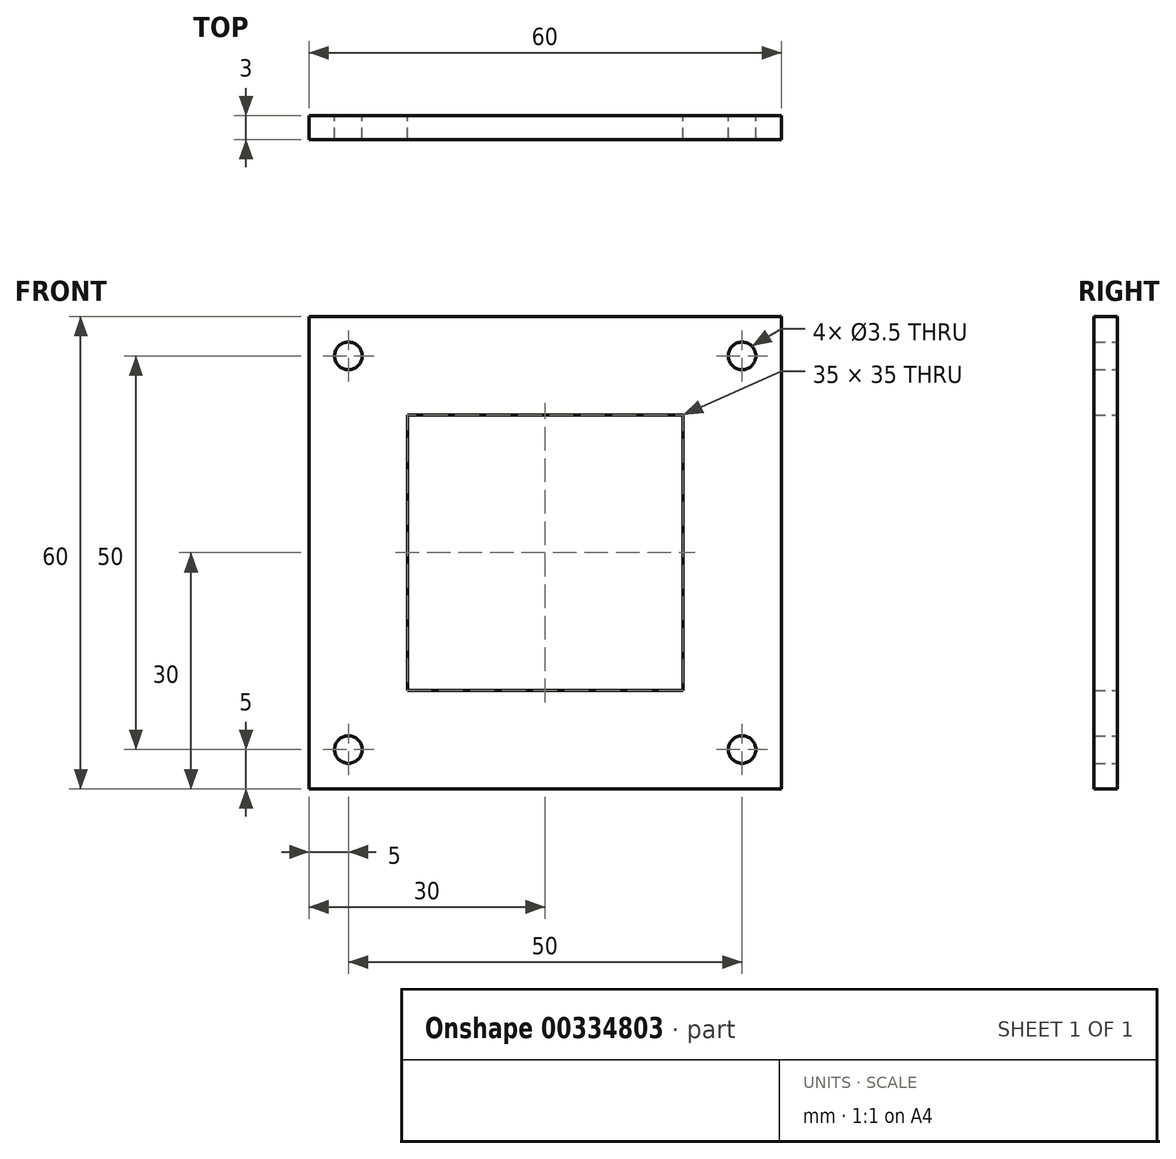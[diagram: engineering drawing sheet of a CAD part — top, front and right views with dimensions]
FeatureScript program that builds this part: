
annotation { "Feature Type Name" : "Feature", "Feature Type Description" : "" }
export const myFeature = defineFeature(function(context is Context, id is Id, definition is map)
    precondition{}
    {
        {
            var Q0;
            Q0=qCreatedBy(makeId("Front.planeOp"),FACE);
            var sketch = newSketch(context, id + "F0", { "sketchPlane" : qUnion([Q0])});
            skLineSegment(sketch, "E0.bottom", {"start": v(30, -30) * mm, "end": v(-30, -30) * mm});
            skLineSegment(sketch, "E0.top", {"start": v(30, 30) * mm, "end": v(-30, 30) * mm});
            skLineSegment(sketch, "E0.left", {"start": v(30, -30) * mm, "end": v(30, 30) * mm});
            skLineSegment(sketch, "E0.right", {"start": v(-30, -30) * mm, "end": v(-30, 30) * mm});
            skPoint(sketch, "E0.middle", {"position": v(0, 0) * mm});
            skLineSegment(sketch, "E1.bottom", {"start": v(17.5, -17.5) * mm, "end": v(-17.5, -17.5) * mm});
            skLineSegment(sketch, "E1.top", {"start": v(17.5, 17.5) * mm, "end": v(-17.5, 17.5) * mm});
            skLineSegment(sketch, "E1.left", {"start": v(17.5, -17.5) * mm, "end": v(17.5, 17.5) * mm});
            skLineSegment(sketch, "E1.right", {"start": v(-17.5, -17.5) * mm, "end": v(-17.5, 17.5) * mm});
            skCircle(sketch, "E2", {"center": v(-25, 25) * mm, "radius": 1.75 * mm});
            skCircle(sketch, "E3", {"center": v(-25, -25) * mm, "radius": 1.75 * mm});
            skCircle(sketch, "E4", {"center": v(25, 25) * mm, "radius": 1.75 * mm});
            skCircle(sketch, "E5", {"center": v(25, -25) * mm, "radius": 1.75 * mm});
            skSolve(sketch);
        }
        {
            var Q0;
            Q0=makeQuery(id+"F0.imprint","IMPRINT",FACE,{"disambiguationData":[TD([[makeQuery(id+"F0.imprint","IMPRINT",EDGE,{"derivedFrom":sQuery(id+"F0.wireOp",EDGE,"E0.bottom")}),-1.0]])]});
            extrude(context, id + "F1", {"entities" : qUnion([Q0]), "depth" : 3 * mm});
        }
    });
